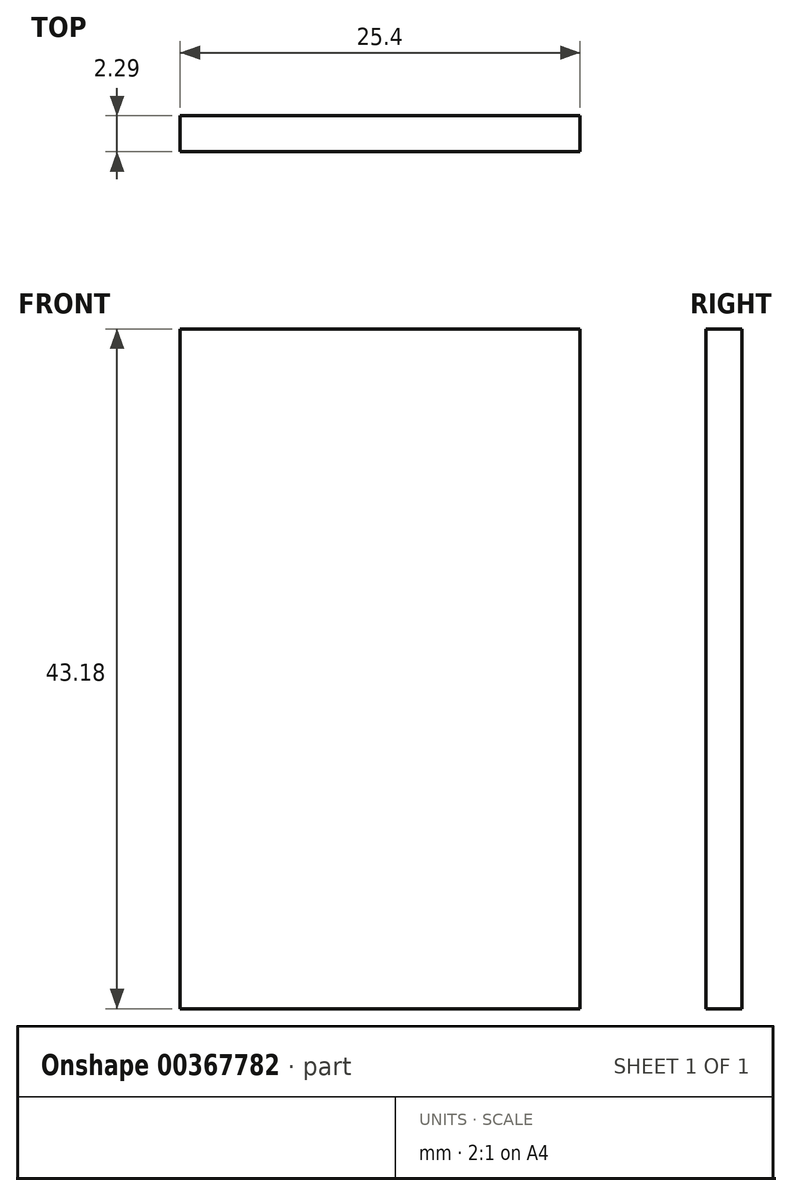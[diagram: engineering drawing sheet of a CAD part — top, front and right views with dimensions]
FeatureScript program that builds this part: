
annotation { "Feature Type Name" : "Feature", "Feature Type Description" : "" }
export const myFeature = defineFeature(function(context is Context, id is Id, definition is map)
    precondition{}
    {
        {
            var Q0;
            Q0=qCreatedBy(makeId("Front.planeOp"),FACE);
            var sketch = newSketch(context, id + "F0", { "sketchPlane" : qUnion([Q0])});
            skLineSegment(sketch, "E0.bottom", {"start": v(-62.25, 32.73) * mm, "end": v(-36.85, 32.73) * mm});
            skLineSegment(sketch, "E0.top", {"start": v(-62.25, -10.45) * mm, "end": v(-36.85, -10.45) * mm});
            skLineSegment(sketch, "E0.left", {"start": v(-62.25, 32.73) * mm, "end": v(-62.25, -10.45) * mm});
            skLineSegment(sketch, "E0.right", {"start": v(-36.85, 32.73) * mm, "end": v(-36.85, -10.45) * mm});
            skSolve(sketch);
        }
        {
            var Q0;
            Q0 = qSketchRegion(id + "F0", true);
            extrude(context, id + "F1", {"entities" : qUnion([Q0]), "depth" : 2.3 * mm});
        }
    });
